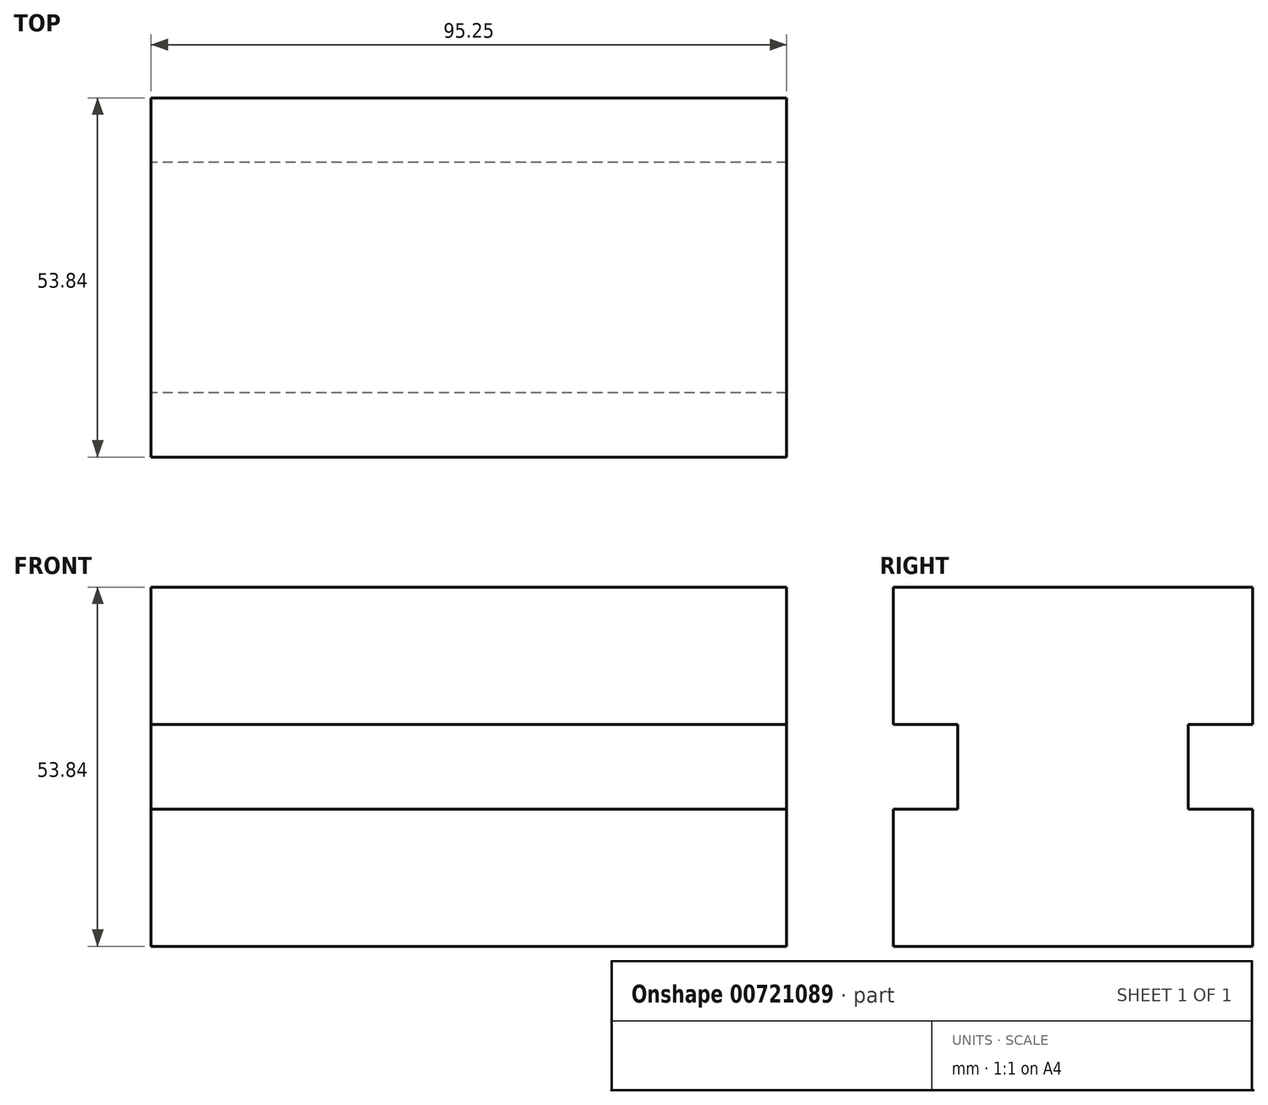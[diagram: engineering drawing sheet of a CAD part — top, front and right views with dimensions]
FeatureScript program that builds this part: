
annotation { "Feature Type Name" : "Feature", "Feature Type Description" : "" }
export const myFeature = defineFeature(function(context is Context, id is Id, definition is map)
    precondition{}
    {
        {
            var Q0;
            Q0=qCreatedBy(makeId("Right.planeOp"),FACE);
            var sketch = newSketch(context, id + "F0", { "sketchPlane" : qUnion([Q0])});
            skLineSegment(sketch, "E0.bottom", {"start": v(26.92, -26.92) * mm, "end": v(-26.92, -26.92) * mm});
            skLineSegment(sketch, "E0.top", {"start": v(26.92, 26.92) * mm, "end": v(-26.92, 26.92) * mm});
            skLineSegment(sketch, "E0.left", {"start": v(26.92, -26.92) * mm, "end": v(26.92, -6.35) * mm});
            skLineSegment(sketch, "E0.right", {"start": v(-26.92, -26.92) * mm, "end": v(-26.92, -6.35) * mm});
            skPoint(sketch, "E0.middle", {"position": v(0, 0) * mm});
            skLineSegment(sketch, "E1.bottom", {"start": v(-26.92, 6.35) * mm, "end": v(-17.27, 6.35) * mm});
            skLineSegment(sketch, "E1.top", {"start": v(-26.92, -6.35) * mm, "end": v(-17.27, -6.35) * mm});
            skLineSegment(sketch, "E1.right", {"start": v(-17.27, 6.35) * mm, "end": v(-17.27, -6.35) * mm});
            skLineSegment(sketch, "E2", {"start": v(0, 42.91) * mm, "end": v(0, -46.17) * mm, "construction": true});
            skPoint(sketch, "E2.startSnap0", {"position": v(0, 26.92) * mm});
            skLineSegment(sketch, "E3.MirrorCS", {"start": v(26.92, 6.35) * mm, "end": v(17.27, 6.35) * mm});
            skLineSegment(sketch, "E4.MirrorCS", {"start": v(17.27, 6.35) * mm, "end": v(17.27, -6.35) * mm});
            skLineSegment(sketch, "E5.MirrorCS", {"start": v(26.92, -6.35) * mm, "end": v(17.27, -6.35) * mm});
            skLineSegment(sketch, "E6.trimOffspring", {"start": v(-26.92, 6.35) * mm, "end": v(-26.92, 26.92) * mm});
            skLineSegment(sketch, "E7.trimOffspring", {"start": v(26.92, 6.35) * mm, "end": v(26.92, 26.92) * mm});
            skSolve(sketch);
        }
        {
            var Q0;
            Q0=makeQuery(id+"F0.imprint","IMPRINT",FACE,{"disambiguationData":[TD([[makeQuery(id+"F0.imprint","IMPRINT",EDGE,{"derivedFrom":sQuery(id+"F0.wireOp",EDGE,"E0.bottom")}),-1.0]])]});
            extrude(context, id + "F1", {"entities" : qUnion([Q0]), "depth" : 95.25 * mm, "offsetDistance" : 25.4 * mm});
        }
    });
